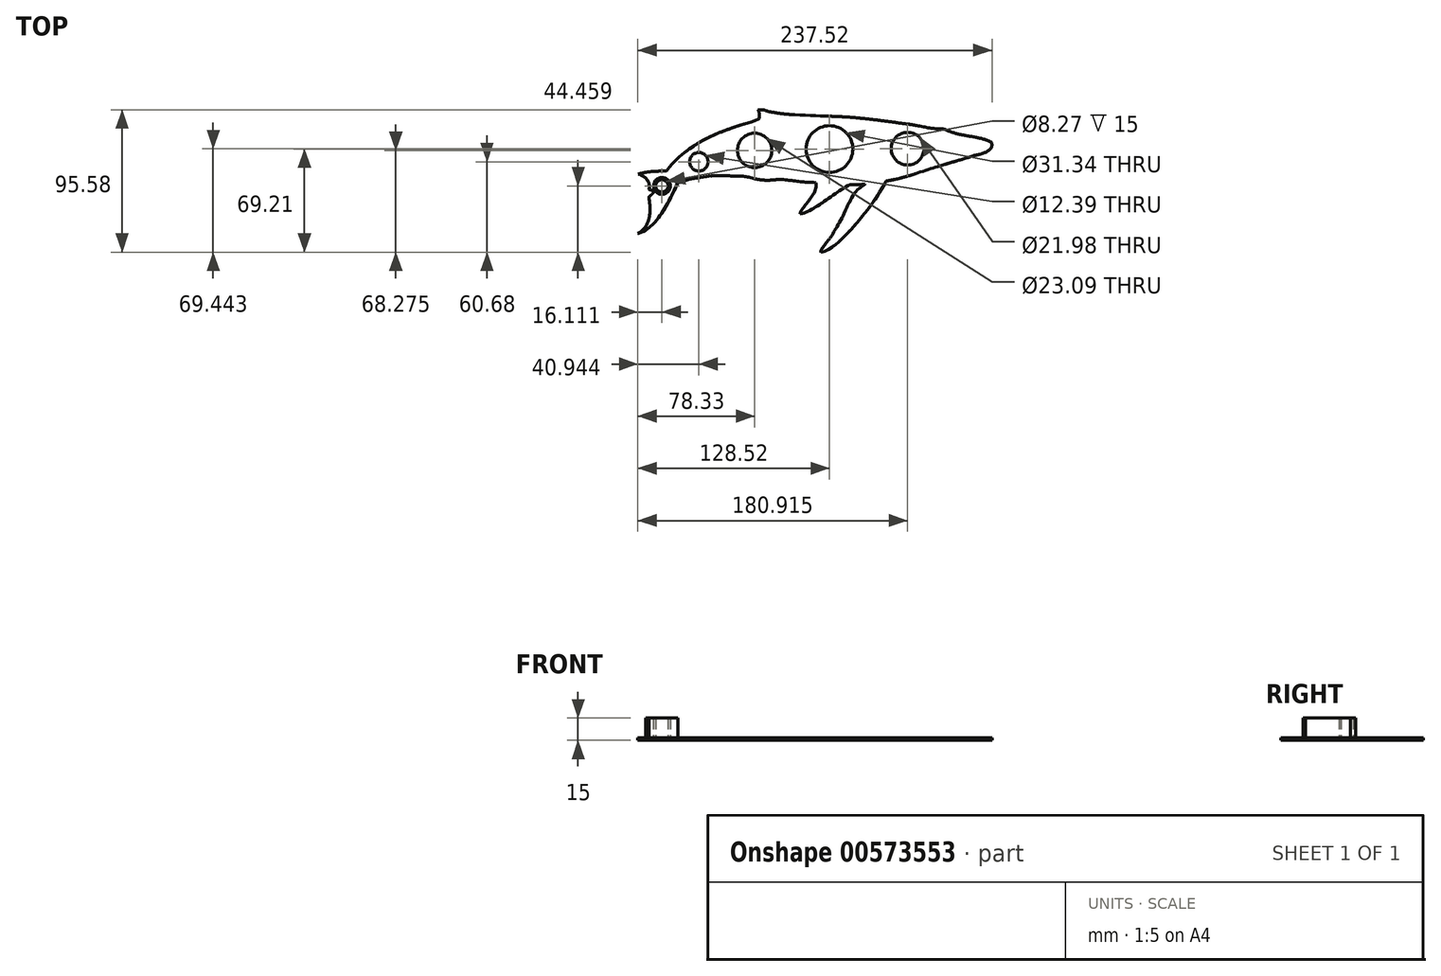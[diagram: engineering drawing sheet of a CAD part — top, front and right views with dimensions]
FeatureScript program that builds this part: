
annotation { "Feature Type Name" : "Feature", "Feature Type Description" : "" }
export const myFeature = defineFeature(function(context is Context, id is Id, definition is map)
    precondition{}
    {
        {
            var Q0;
            Q0=qCreatedBy(makeId("Top.planeOp"),FACE);
            var sketch = newSketch(context, id + "F0", { "sketchPlane" : qUnion([Q0])});
            skFitSpline(sketch, "E0", {"points": [v(-110.19, 0) * mm, v(-48.5, 34.69) * mm], "startDerivative": vector(57.6, 77) * mm, "endDerivative": vector(16.2, 9.67) * mm});
            skFitSpline(sketch, "E1", {"points": [v(-48.5, 34.69) * mm, v(-50.34, 40.18) * mm], "startDerivative": vector(0.72, 1.62) * mm, "endDerivative": vector(-5.5, 2.54) * mm});
            skFitSpline(sketch, "E2", {"points": [v(-50.34, 40.18) * mm, v(-43.24, 40.8) * mm], "startDerivative": vector(-2.73, 4.03) * mm, "endDerivative": vector(2.34, -1.43) * mm});
            skFitSpline(sketch, "E3", {"points": [v(-43.24, 40.8) * mm, v(-26.6, 38.04) * mm], "startDerivative": vector(7.14, -3.25) * mm, "endDerivative": vector(17.79, -1.17) * mm});
            skFitSpline(sketch, "E4", {"points": [v(-26.6, 38.04) * mm, v(52.76, 31.52) * mm], "startDerivative": vector(118.04, -6.61) * mm, "endDerivative": vector(139.6, -19.33) * mm});
            skFitSpline(sketch, "E5", {"points": [v(52.76, 31.52) * mm, v(76.5, 28.51) * mm], "startDerivative": vector(27.44, -3.59) * mm, "endDerivative": vector(22.06, 2.06) * mm});
            skFitSpline(sketch, "E6", {"points": [v(76.5, 28.51) * mm, v(91.7, 23.84) * mm], "startDerivative": vector(12.9, -6.17) * mm, "endDerivative": vector(17.2, -2.8) * mm});
            skFitSpline(sketch, "E7", {"points": [v(91.7, 23.84) * mm, v(110.4, 17.5) * mm], "startDerivative": vector(32.3, -4.92) * mm, "endDerivative": vector(-1.24, -7.06) * mm});
            skFitSpline(sketch, "E8", {"points": [v(110.4, 17.5) * mm, v(97.52, 7.5) * mm], "startDerivative": vector(-0.35, -4.06) * mm, "endDerivative": vector(-46.06, -8.82) * mm});
            skFitSpline(sketch, "E9", {"points": [v(97.52, 7.5) * mm, v(58.17, -4.68) * mm], "startDerivative": vector(-43.94, -13.76) * mm, "endDerivative": vector(-40.24, -14.05) * mm});
            skFitSpline(sketch, "E10", {"points": [v(58.17, -4.68) * mm, v(38.92, -9.55) * mm], "startDerivative": vector(-20.92, -6.62) * mm, "endDerivative": vector(-21.3, -3.64) * mm});
            skFitSpline(sketch, "E11", {"points": [v(38.92, -9.55) * mm, v(-6.23, -57.37) * mm], "startDerivative": vector(-23.21, -46.88) * mm, "endDerivative": vector(-31.45, 2.9) * mm});
            skFitSpline(sketch, "E12", {"points": [v(-6.23, -57.37) * mm, v(2.23, -40.45) * mm], "startDerivative": vector(-14.35, 5.09) * mm, "endDerivative": vector(6.68, 17.66) * mm});
            skFitSpline(sketch, "E13", {"points": [v(2.23, -40.45) * mm, v(18.71, -12.13) * mm], "startDerivative": vector(19.53, 28.38) * mm, "endDerivative": vector(17.77, 12.91) * mm});
            skFitSpline(sketch, "E14", {"points": [v(18.71, -12.13) * mm, v(13.96, -12.13) * mm], "startDerivative": vector(-3.78, -0.25) * mm, "endDerivative": vector(-4.66, 0.42) * mm});
            skFitSpline(sketch, "E15", {"points": [v(13.96, -12.13) * mm, v(-20.4, -31.66) * mm], "startDerivative": vector(-17.49, -6.42) * mm, "endDerivative": vector(-19.66, 4.33) * mm});
            skFitSpline(sketch, "E16", {"points": [v(-20.4, -31.66) * mm, v(-10.58, -10.63) * mm], "startDerivative": vector(-13.32, 9.81) * mm, "endDerivative": vector(-4.9, 18.93) * mm});
            skFitSpline(sketch, "E17", {"points": [v(-10.58, -10.63) * mm, v(-34.92, -8.62) * mm], "startDerivative": vector(-38.59, 1.09) * mm, "endDerivative": vector(-9.75, -2.04) * mm});
            skFitSpline(sketch, "E18", {"points": [v(-34.92, -8.62) * mm, v(-57.99, -6.48) * mm], "startDerivative": vector(-39.05, -5.06) * mm, "endDerivative": vector(-19.99, 2) * mm});
            skFitSpline(sketch, "E19", {"points": [v(-57.99, -6.48) * mm, v(-100.65, -10.47) * mm], "startDerivative": vector(-30.29, -1.49) * mm, "endDerivative": vector(-77.37, -21.71) * mm});
            skFitSpline(sketch, "E20", {"points": [v(-100.65, -10.47) * mm, v(-132.83, -45.13) * mm], "startDerivative": vector(-26.95, -59.15) * mm, "endDerivative": vector(-41.01, 2.75) * mm});
            skFitSpline(sketch, "E21", {"points": [v(-132.83, -45.13) * mm, v(-122.68, -18.64) * mm], "startDerivative": vector(9.55, 15.23) * mm, "endDerivative": vector(-10.84, 69.28) * mm});
            skFitSpline(sketch, "E22", {"points": [v(-122.68, -18.64) * mm, v(-119.9, -15.76) * mm], "startDerivative": vector(0.53, 4.23) * mm, "endDerivative": vector(1.94, 2.9) * mm});
            skFitSpline(sketch, "E23", {"points": [v(-119.9, -15.76) * mm, v(-122.77, -14.59) * mm], "startDerivative": vector(-1.85, 0.8) * mm, "endDerivative": vector(-1.85, 2.12) * mm});
            skFitSpline(sketch, "E24", {"points": [v(-122.77, -14.59) * mm, v(-132.83, -3.75) * mm], "startDerivative": vector(8.46, 27.23) * mm, "endDerivative": vector(-4.97, 2.2) * mm});
            skCircle(sketch, "E25", {"center": v(-87.58, 4.8) * mm, "radius": 4.7 * mm});
            skCircle(sketch, "E26", {"center": v(-50.2, 12.39) * mm, "radius": 10.05 * mm});
            skCircle(sketch, "E27", {"center": v(0, 13.32) * mm, "radius": 14.17 * mm});
            skCircle(sketch, "E28", {"center": v(52.4, 13.55) * mm, "radius": 9.49 * mm});
            skCircle(sketch, "E29", {"center": v(-112.4, -11.43) * mm, "radius": 4.13 * mm});
            skFitSpline(sketch, "E30", {"points": [v(-132.83, -3.75) * mm, v(-110.19, 0) * mm], "startDerivative": vector(22.86, 11.25) * mm, "endDerivative": vector(20.27, 0) * mm});
            skSolve(sketch);
        }
        {
            var Q0;
            Q0=makeQuery(id+"F0.imprint","IMPRINT",FACE,{"disambiguationData":[TD([[makeQuery(id+"F0.imprint","IMPRINT",EDGE,{"derivedFrom":sQuery(id+"F0.wireOp",EDGE,"E0")}),-1.0]])]});
            extrude(context, id + "F1", {"entities" : qUnion([Q0]), "depth" : 15 * mm, "offsetDistance" : 25.4 * mm});
        }
        {
            var Q0;
            Q0=makeQuery(id+"F1.opExtrude","CAP_FACE",FACE,{"disambiguationData":[OSD([sQuery(id+"F0.wireOp",EDGE,"E0"),sQuery(id+"F0.wireOp",EDGE,"a87ef808-fcfc-4c1f-a108-a0a01820a8e6"),sQuery(id+"F0.wireOp",EDGE,"E1"),sQuery(id+"F0.wireOp",EDGE,"E2"),sQuery(id+"F0.wireOp",EDGE,"E3"),sQuery(id+"F0.wireOp",EDGE,"E4"),sQuery(id+"F0.wireOp",EDGE,"E5"),sQuery(id+"F0.wireOp",EDGE,"E6"),sQuery(id+"F0.wireOp",EDGE,"E7"),sQuery(id+"F0.wireOp",EDGE,"E8"),sQuery(id+"F0.wireOp",EDGE,"E9"),sQuery(id+"F0.wireOp",EDGE,"E10"),sQuery(id+"F0.wireOp",EDGE,"E11"),sQuery(id+"F0.wireOp",EDGE,"E12"),sQuery(id+"F0.wireOp",EDGE,"E13"),sQuery(id+"F0.wireOp",EDGE,"E14"),sQuery(id+"F0.wireOp",EDGE,"E15"),sQuery(id+"F0.wireOp",EDGE,"E16"),sQuery(id+"F0.wireOp",EDGE,"E17"),sQuery(id+"F0.wireOp",EDGE,"E18"),sQuery(id+"F0.wireOp",EDGE,"E19"),sQuery(id+"F0.wireOp",EDGE,"E20"),sQuery(id+"F0.wireOp",EDGE,"E21"),sQuery(id+"F0.wireOp",EDGE,"E22"),sQuery(id+"F0.wireOp",EDGE,"E23"),sQuery(id+"F0.wireOp",EDGE,"E24")])],"isStart":false});
            shell(context, id + "F2", {"entities" : qUnion([Q0]), "thickness" : 1.5 * mm});
        }
        {
            var Q0;
            {var subQ0=sQuery(id+"F0.wireOp",EDGE,"E29");var subQ1=sQuery(id+"F0.wireOp",EDGE,"E28");var subQ2=sQuery(id+"F0.wireOp",EDGE,"E27");var subQ3=sQuery(id+"F0.wireOp",EDGE,"E26");var subQ4=sQuery(id+"F0.wireOp",EDGE,"E25");var subQ5=sQuery(id+"F0.wireOp",EDGE,"E24");var subQ6=sQuery(id+"F0.wireOp",EDGE,"E23");var subQ7=sQuery(id+"F0.wireOp",EDGE,"E22");var subQ8=sQuery(id+"F0.wireOp",EDGE,"E21");var subQ9=sQuery(id+"F0.wireOp",EDGE,"E20");var subQ10=sQuery(id+"F0.wireOp",EDGE,"E19");var subQ11=sQuery(id+"F0.wireOp",EDGE,"E18");var subQ12=sQuery(id+"F0.wireOp",EDGE,"E17");var subQ13=sQuery(id+"F0.wireOp",EDGE,"E16");var subQ14=sQuery(id+"F0.wireOp",EDGE,"E15");var subQ15=sQuery(id+"F0.wireOp",EDGE,"E14");var subQ16=sQuery(id+"F0.wireOp",EDGE,"E13");var subQ17=sQuery(id+"F0.wireOp",EDGE,"E12");var subQ18=sQuery(id+"F0.wireOp",EDGE,"E11");var subQ19=sQuery(id+"F0.wireOp",EDGE,"E10");var subQ20=sQuery(id+"F0.wireOp",EDGE,"E9");var subQ21=sQuery(id+"F0.wireOp",EDGE,"E8");var subQ22=sQuery(id+"F0.wireOp",EDGE,"E7");var subQ23=sQuery(id+"F0.wireOp",EDGE,"E6");var subQ24=sQuery(id+"F0.wireOp",EDGE,"E5");var subQ25=sQuery(id+"F0.wireOp",EDGE,"E4");var subQ26=sQuery(id+"F0.wireOp",EDGE,"E3");var subQ27=sQuery(id+"F0.wireOp",EDGE,"E2");var subQ28=sQuery(id+"F0.wireOp",EDGE,"E1");var subQ29=sQuery(id+"F0.wireOp",EDGE,"a87ef808-fcfc-4c1f-a108-a0a01820a8e6");var subQ30=sQuery(id+"F0.wireOp",EDGE,"E0");Q0=makeQuery(id+"F2.opShell","OFFSET_FACE",FACE,{"disambiguationData":[OSD([subQ30,subQ29,subQ28,subQ27,subQ26,subQ25,subQ24,subQ23,subQ22,subQ21,subQ20,subQ19,subQ18,subQ17,subQ16,subQ15,subQ14,subQ13,subQ12,subQ11,subQ10,subQ9,subQ8,subQ7,subQ6,subQ5,subQ4,subQ3,subQ2,subQ1,subQ0]),TDD([makeQuery(id+"F1.opExtrude","CAP_FACE",FACE,{"disambiguationData":[OSD([subQ30,subQ29,subQ28,subQ27,subQ26,subQ25,subQ24,subQ23,subQ22,subQ21,subQ20,subQ19,subQ18,subQ17,subQ16,subQ15,subQ14,subQ13,subQ12,subQ11,subQ10,subQ9,subQ8,subQ7,subQ6,subQ5,subQ4,subQ3,subQ2,subQ1,subQ0])],"isStart":false})]),OD(2.0)]});}
            var Q1;
            {var subQ0=sQuery(id+"F0.wireOp",EDGE,"E29");var subQ1=sQuery(id+"F0.wireOp",EDGE,"E28");var subQ2=sQuery(id+"F0.wireOp",EDGE,"E27");var subQ3=sQuery(id+"F0.wireOp",EDGE,"E26");var subQ4=sQuery(id+"F0.wireOp",EDGE,"E25");var subQ5=sQuery(id+"F0.wireOp",EDGE,"E24");var subQ6=sQuery(id+"F0.wireOp",EDGE,"E23");var subQ7=sQuery(id+"F0.wireOp",EDGE,"E22");var subQ8=sQuery(id+"F0.wireOp",EDGE,"E21");var subQ9=sQuery(id+"F0.wireOp",EDGE,"E20");var subQ10=sQuery(id+"F0.wireOp",EDGE,"E19");var subQ11=sQuery(id+"F0.wireOp",EDGE,"E18");var subQ12=sQuery(id+"F0.wireOp",EDGE,"E17");var subQ13=sQuery(id+"F0.wireOp",EDGE,"E16");var subQ14=sQuery(id+"F0.wireOp",EDGE,"E15");var subQ15=sQuery(id+"F0.wireOp",EDGE,"E14");var subQ16=sQuery(id+"F0.wireOp",EDGE,"E13");var subQ17=sQuery(id+"F0.wireOp",EDGE,"E12");var subQ18=sQuery(id+"F0.wireOp",EDGE,"E11");var subQ19=sQuery(id+"F0.wireOp",EDGE,"E10");var subQ20=sQuery(id+"F0.wireOp",EDGE,"E9");var subQ21=sQuery(id+"F0.wireOp",EDGE,"E8");var subQ22=sQuery(id+"F0.wireOp",EDGE,"E7");var subQ23=sQuery(id+"F0.wireOp",EDGE,"E6");var subQ24=sQuery(id+"F0.wireOp",EDGE,"E5");var subQ25=sQuery(id+"F0.wireOp",EDGE,"E4");var subQ26=sQuery(id+"F0.wireOp",EDGE,"E3");var subQ27=sQuery(id+"F0.wireOp",EDGE,"E2");var subQ28=sQuery(id+"F0.wireOp",EDGE,"E1");var subQ29=sQuery(id+"F0.wireOp",EDGE,"a87ef808-fcfc-4c1f-a108-a0a01820a8e6");var subQ30=sQuery(id+"F0.wireOp",EDGE,"E0");Q1=makeQuery(id+"F2.opShell","OFFSET_FACE",FACE,{"disambiguationData":[OSD([subQ30,subQ29,subQ28,subQ27,subQ26,subQ25,subQ24,subQ23,subQ22,subQ21,subQ20,subQ19,subQ18,subQ17,subQ16,subQ15,subQ14,subQ13,subQ12,subQ11,subQ10,subQ9,subQ8,subQ7,subQ6,subQ5,subQ4,subQ3,subQ2,subQ1,subQ0]),TDD([makeQuery(id+"F1.opExtrude","CAP_FACE",FACE,{"disambiguationData":[OSD([subQ30,subQ29,subQ28,subQ27,subQ26,subQ25,subQ24,subQ23,subQ22,subQ21,subQ20,subQ19,subQ18,subQ17,subQ16,subQ15,subQ14,subQ13,subQ12,subQ11,subQ10,subQ9,subQ8,subQ7,subQ6,subQ5,subQ4,subQ3,subQ2,subQ1,subQ0])],"isStart":false})]),OD(1.0)]});}
            var Q2;
            {var subQ0=sQuery(id+"F0.wireOp",EDGE,"E29");var subQ1=sQuery(id+"F0.wireOp",EDGE,"E28");var subQ2=sQuery(id+"F0.wireOp",EDGE,"E27");var subQ3=sQuery(id+"F0.wireOp",EDGE,"E26");var subQ4=sQuery(id+"F0.wireOp",EDGE,"E25");var subQ5=sQuery(id+"F0.wireOp",EDGE,"E24");var subQ6=sQuery(id+"F0.wireOp",EDGE,"E23");var subQ7=sQuery(id+"F0.wireOp",EDGE,"E22");var subQ8=sQuery(id+"F0.wireOp",EDGE,"E21");var subQ9=sQuery(id+"F0.wireOp",EDGE,"E20");var subQ10=sQuery(id+"F0.wireOp",EDGE,"E19");var subQ11=sQuery(id+"F0.wireOp",EDGE,"E18");var subQ12=sQuery(id+"F0.wireOp",EDGE,"E17");var subQ13=sQuery(id+"F0.wireOp",EDGE,"E16");var subQ14=sQuery(id+"F0.wireOp",EDGE,"E15");var subQ15=sQuery(id+"F0.wireOp",EDGE,"E14");var subQ16=sQuery(id+"F0.wireOp",EDGE,"E13");var subQ17=sQuery(id+"F0.wireOp",EDGE,"E12");var subQ18=sQuery(id+"F0.wireOp",EDGE,"E11");var subQ19=sQuery(id+"F0.wireOp",EDGE,"E10");var subQ20=sQuery(id+"F0.wireOp",EDGE,"E9");var subQ21=sQuery(id+"F0.wireOp",EDGE,"E8");var subQ22=sQuery(id+"F0.wireOp",EDGE,"E7");var subQ23=sQuery(id+"F0.wireOp",EDGE,"E6");var subQ24=sQuery(id+"F0.wireOp",EDGE,"E5");var subQ25=sQuery(id+"F0.wireOp",EDGE,"E4");var subQ26=sQuery(id+"F0.wireOp",EDGE,"E3");var subQ27=sQuery(id+"F0.wireOp",EDGE,"E2");var subQ28=sQuery(id+"F0.wireOp",EDGE,"E1");var subQ29=sQuery(id+"F0.wireOp",EDGE,"a87ef808-fcfc-4c1f-a108-a0a01820a8e6");var subQ30=sQuery(id+"F0.wireOp",EDGE,"E0");Q2=makeQuery(id+"F2.opShell","OFFSET_FACE",FACE,{"disambiguationData":[OSD([subQ30,subQ29,subQ28,subQ27,subQ26,subQ25,subQ24,subQ23,subQ22,subQ21,subQ20,subQ19,subQ18,subQ17,subQ16,subQ15,subQ14,subQ13,subQ12,subQ11,subQ10,subQ9,subQ8,subQ7,subQ6,subQ5,subQ4,subQ3,subQ2,subQ1,subQ0]),TDD([makeQuery(id+"F1.opExtrude","CAP_FACE",FACE,{"disambiguationData":[OSD([subQ30,subQ29,subQ28,subQ27,subQ26,subQ25,subQ24,subQ23,subQ22,subQ21,subQ20,subQ19,subQ18,subQ17,subQ16,subQ15,subQ14,subQ13,subQ12,subQ11,subQ10,subQ9,subQ8,subQ7,subQ6,subQ5,subQ4,subQ3,subQ2,subQ1,subQ0])],"isStart":false})]),OD(3.0)]});}
            var Q3;
            {var subQ0=sQuery(id+"F0.wireOp",EDGE,"E29");var subQ1=sQuery(id+"F0.wireOp",EDGE,"E28");var subQ2=sQuery(id+"F0.wireOp",EDGE,"E27");var subQ3=sQuery(id+"F0.wireOp",EDGE,"E26");var subQ4=sQuery(id+"F0.wireOp",EDGE,"E25");var subQ5=sQuery(id+"F0.wireOp",EDGE,"E24");var subQ6=sQuery(id+"F0.wireOp",EDGE,"E23");var subQ7=sQuery(id+"F0.wireOp",EDGE,"E22");var subQ8=sQuery(id+"F0.wireOp",EDGE,"E21");var subQ9=sQuery(id+"F0.wireOp",EDGE,"E20");var subQ10=sQuery(id+"F0.wireOp",EDGE,"E19");var subQ11=sQuery(id+"F0.wireOp",EDGE,"E18");var subQ12=sQuery(id+"F0.wireOp",EDGE,"E17");var subQ13=sQuery(id+"F0.wireOp",EDGE,"E16");var subQ14=sQuery(id+"F0.wireOp",EDGE,"E15");var subQ15=sQuery(id+"F0.wireOp",EDGE,"E14");var subQ16=sQuery(id+"F0.wireOp",EDGE,"E13");var subQ17=sQuery(id+"F0.wireOp",EDGE,"E12");var subQ18=sQuery(id+"F0.wireOp",EDGE,"E11");var subQ19=sQuery(id+"F0.wireOp",EDGE,"E10");var subQ20=sQuery(id+"F0.wireOp",EDGE,"E9");var subQ21=sQuery(id+"F0.wireOp",EDGE,"E8");var subQ22=sQuery(id+"F0.wireOp",EDGE,"E7");var subQ23=sQuery(id+"F0.wireOp",EDGE,"E6");var subQ24=sQuery(id+"F0.wireOp",EDGE,"E5");var subQ25=sQuery(id+"F0.wireOp",EDGE,"E4");var subQ26=sQuery(id+"F0.wireOp",EDGE,"E3");var subQ27=sQuery(id+"F0.wireOp",EDGE,"E2");var subQ28=sQuery(id+"F0.wireOp",EDGE,"E1");var subQ29=sQuery(id+"F0.wireOp",EDGE,"a87ef808-fcfc-4c1f-a108-a0a01820a8e6");var subQ30=sQuery(id+"F0.wireOp",EDGE,"E0");Q3=makeQuery(id+"F2.opShell","OFFSET_FACE",FACE,{"disambiguationData":[OSD([subQ30,subQ29,subQ28,subQ27,subQ26,subQ25,subQ24,subQ23,subQ22,subQ21,subQ20,subQ19,subQ18,subQ17,subQ16,subQ15,subQ14,subQ13,subQ12,subQ11,subQ10,subQ9,subQ8,subQ7,subQ6,subQ5,subQ4,subQ3,subQ2,subQ1,subQ0]),TDD([makeQuery(id+"F1.opExtrude","CAP_FACE",FACE,{"disambiguationData":[OSD([subQ30,subQ29,subQ28,subQ27,subQ26,subQ25,subQ24,subQ23,subQ22,subQ21,subQ20,subQ19,subQ18,subQ17,subQ16,subQ15,subQ14,subQ13,subQ12,subQ11,subQ10,subQ9,subQ8,subQ7,subQ6,subQ5,subQ4,subQ3,subQ2,subQ1,subQ0])],"isStart":false})]),OD(0.0)]});}
            var Q4;
            {var subQ0=sQuery(id+"F0.wireOp",EDGE,"E29");var subQ1=sQuery(id+"F0.wireOp",EDGE,"E28");var subQ2=sQuery(id+"F0.wireOp",EDGE,"E27");var subQ3=sQuery(id+"F0.wireOp",EDGE,"E26");var subQ4=sQuery(id+"F0.wireOp",EDGE,"E25");var subQ5=sQuery(id+"F0.wireOp",EDGE,"E24");var subQ6=sQuery(id+"F0.wireOp",EDGE,"E23");var subQ7=sQuery(id+"F0.wireOp",EDGE,"E22");var subQ8=sQuery(id+"F0.wireOp",EDGE,"E21");var subQ9=sQuery(id+"F0.wireOp",EDGE,"E20");var subQ10=sQuery(id+"F0.wireOp",EDGE,"E19");var subQ11=sQuery(id+"F0.wireOp",EDGE,"E18");var subQ12=sQuery(id+"F0.wireOp",EDGE,"E17");var subQ13=sQuery(id+"F0.wireOp",EDGE,"E16");var subQ14=sQuery(id+"F0.wireOp",EDGE,"E15");var subQ15=sQuery(id+"F0.wireOp",EDGE,"E14");var subQ16=sQuery(id+"F0.wireOp",EDGE,"E13");var subQ17=sQuery(id+"F0.wireOp",EDGE,"E12");var subQ18=sQuery(id+"F0.wireOp",EDGE,"E11");var subQ19=sQuery(id+"F0.wireOp",EDGE,"E10");var subQ20=sQuery(id+"F0.wireOp",EDGE,"E9");var subQ21=sQuery(id+"F0.wireOp",EDGE,"E8");var subQ22=sQuery(id+"F0.wireOp",EDGE,"E7");var subQ23=sQuery(id+"F0.wireOp",EDGE,"E6");var subQ24=sQuery(id+"F0.wireOp",EDGE,"E5");var subQ25=sQuery(id+"F0.wireOp",EDGE,"E4");var subQ26=sQuery(id+"F0.wireOp",EDGE,"E3");var subQ27=sQuery(id+"F0.wireOp",EDGE,"E2");var subQ28=sQuery(id+"F0.wireOp",EDGE,"E1");var subQ29=sQuery(id+"F0.wireOp",EDGE,"a87ef808-fcfc-4c1f-a108-a0a01820a8e6");var subQ30=sQuery(id+"F0.wireOp",EDGE,"E0");Q4=makeQuery(id+"F2.opShell","OFFSET_FACE",FACE,{"disambiguationData":[OSD([subQ30,subQ29,subQ28,subQ27,subQ26,subQ25,subQ24,subQ23,subQ22,subQ21,subQ20,subQ19,subQ18,subQ17,subQ16,subQ15,subQ14,subQ13,subQ12,subQ11,subQ10,subQ9,subQ8,subQ7,subQ6,subQ5,subQ4,subQ3,subQ2,subQ1,subQ0]),TDD([makeQuery(id+"F1.opExtrude","CAP_FACE",FACE,{"disambiguationData":[OSD([subQ30,subQ29,subQ28,subQ27,subQ26,subQ25,subQ24,subQ23,subQ22,subQ21,subQ20,subQ19,subQ18,subQ17,subQ16,subQ15,subQ14,subQ13,subQ12,subQ11,subQ10,subQ9,subQ8,subQ7,subQ6,subQ5,subQ4,subQ3,subQ2,subQ1,subQ0])],"isStart":false})]),OD(4.0)]});}
            extrude(context, id + "F3", {"entities" : qUnion([Q0, Q1, Q2, Q3, Q4]), "operationType" : NewBodyOperationType.REMOVE, "oppositeDirection" : true, "depth" : 25 * mm, "offsetDistance" : 25 * mm});
        }
    });
